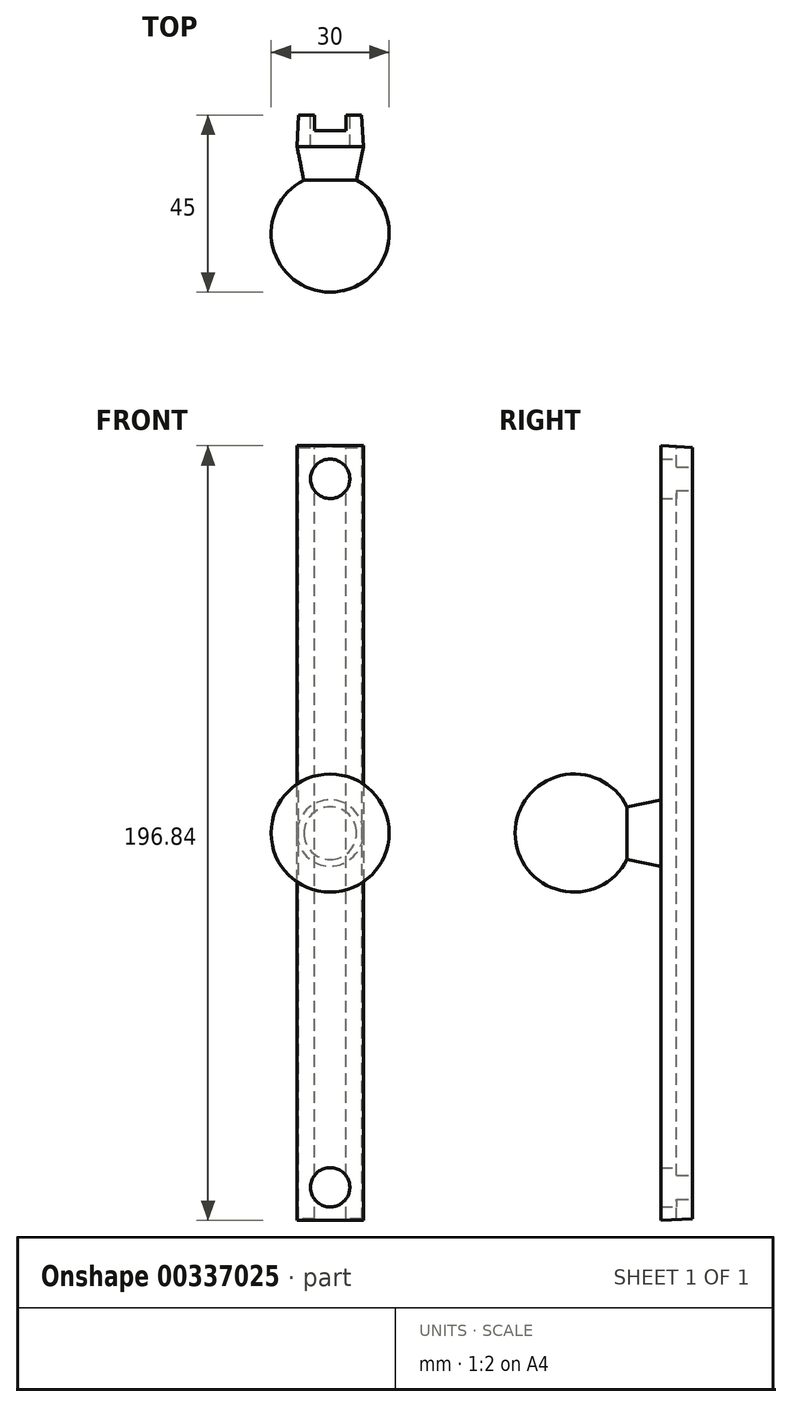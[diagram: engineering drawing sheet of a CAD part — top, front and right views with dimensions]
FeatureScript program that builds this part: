
annotation { "Feature Type Name" : "Feature", "Feature Type Description" : "" }
export const myFeature = defineFeature(function(context is Context, id is Id, definition is map)
    precondition{}
    {
        {
            var Q0;
            Q0=qCreatedBy(makeId("Front.planeOp"),FACE);
            var sketch = newSketch(context, id + "F0", { "sketchPlane" : qUnion([Q0])});
            skLineSegment(sketch, "E0.bottom", {"start": v(8, -98) * mm, "end": v(-8, -98) * mm});
            skLineSegment(sketch, "E0.top", {"start": v(8, 98) * mm, "end": v(-8, 98) * mm});
            skLineSegment(sketch, "E0.left", {"start": v(8, -98) * mm, "end": v(8, 98) * mm});
            skLineSegment(sketch, "E0.right", {"start": v(-8, -98) * mm, "end": v(-8, 98) * mm});
            skPoint(sketch, "E0.middle", {"position": v(0, 0) * mm});
            skSolve(sketch);
        }
        {
            var Q0;
            Q0 = qSketchRegion(id + "F0", true);
            extrude(context, id + "F1", {"entities" : qUnion([Q0]), "depth" : 8 * mm, "hasDraft" : true, "draftAngle" : 3 * degree});
        }
        {
            var Q0;
            Q0 = qSketchRegion(id + "F0", true);
            var sketch = newSketch(context, id + "F2", { "sketchPlane" : qUnion([Q0])});
            skLineSegment(sketch, "E1.bottom", {"start": v(4, -100) * mm, "end": v(-4, -100) * mm});
            skLineSegment(sketch, "E1.top", {"start": v(4, 100) * mm, "end": v(-4, 100) * mm});
            skLineSegment(sketch, "E1.left", {"start": v(4, -100) * mm, "end": v(4, 100) * mm});
            skLineSegment(sketch, "E1.right", {"start": v(-4, -100) * mm, "end": v(-4, 100) * mm});
            skPoint(sketch, "E1.middle", {"position": v(0, 0) * mm});
            skSolve(sketch);
        }
        {
            var Q0;
            Q0 = qSketchRegion(id + "F2", true);
            extrude(context, id + "F3", {"entities" : qUnion([Q0]), "operationType" : NewBodyOperationType.REMOVE, "depth" : 4 * mm});
        }
        {
            var Q0;
            Q0=qCreatedBy(makeId("Front.planeOp"),FACE);
            var sketch = newSketch(context, id + "F4", { "sketchPlane" : qUnion([Q0])});
            skCircle(sketch, "E2", {"center": v(0, 90) * mm, "radius": 5 * mm});
            skCircle(sketch, "E3", {"center": v(0, -90) * mm, "radius": 5 * mm});
            skSolve(sketch);
        }
        {
            var Q0;
            Q0 = qSketchRegion(id + "F4", true);
            extrude(context, id + "F5", {"entities" : qUnion([Q0]), "operationType" : NewBodyOperationType.REMOVE, "depth" : 25.4 * mm});
        }
        {
            var Q0;
            Q0=makeQuery(id+"F1.opExtrude","CAP_FACE",FACE,{"disambiguationData":[OSD([sQuery(id+"F0.wireOp",EDGE,"E0.bottom"),sQuery(id+"F0.wireOp",EDGE,"E0.top"),sQuery(id+"F0.wireOp",EDGE,"E0.left"),sQuery(id+"F0.wireOp",EDGE,"E0.right")])],"isStart":false});
            var sketch = newSketch(context, id + "F6", { "sketchPlane" : qUnion([Q0])});
            skCircle(sketch, "E4", {"center": v(0, 0) * mm, "radius": 8.42 * mm});
            skSolve(sketch);
        }
        {
            var Q0;
            Q0=qCreatedBy(makeId("Front.planeOp"),FACE);
            cPlane(context, id + "F7", {"entities" : qUnion([Q0]), "cplaneType" : CPlaneType.OFFSET, "offset" : 30 * mm, "width" : 152.4 * mm, "height" : 152.4 * mm});
        }
        {
            var Q0;
            Q0=qCreatedBy(id+"F7.planeOp",FACE);
            var sketch = newSketch(context, id + "F8", { "sketchPlane" : qUnion([Q0])});
            skCircle(sketch, "E5", {"center": v(0, 0) * mm, "radius": 4 * mm});
            skSolve(sketch);
        }
        {
            var Q1;
            Q1 = qSketchRegion(id + "F6", true);
            var Q2;
            Q2 = qSketchRegion(id + "F8", true);
            loft(context, id + "F9", {"operationType" : NewBodyOperationType.ADD, "sheetProfilesArray" : [{ "sheetProfileEntities" : qUnion([Q1]) }, { "sheetProfileEntities" : qUnion([Q2]) }]});
        }
        {
            var Q0;
            Q0=qCreatedBy(makeId("Top.planeOp"),FACE);
            var sketch = newSketch(context, id + "F10", { "sketchPlane" : qUnion([Q0])});
            skCircle(sketch, "E6", {"center": v(0, -30) * mm, "radius": 15 * mm, "construction": true});
            skLineSegment(sketch, "E7", {"start": v(0, -15) * mm, "end": v(0, -45) * mm, "construction": true});
            skArc(sketch, "E8", {"start": v(0, -15) * mm, "mid": v(-15, -30) * mm, "end": v(0, -45) * mm});
            skLineSegment(sketch, "E9", {"start": v(0, -15) * mm, "end": v(0, -45) * mm});
            skSolve(sketch);
        }
        {
            var Q0;
            Q0=makeQuery(id+"F10.imprint","IMPRINT",FACE,{"disambiguationData":[TD([[makeQuery(id+"F10.imprint","IMPRINT",EDGE,{"derivedFrom":sQuery(id+"F10.wireOp",EDGE,"E8")}),1.0]])]});
            var Q1;
            Q1=sQuery(id+"F10.wireOp",EDGE,"E9");
            revolve(context, id + "F11", {"operationType" : NewBodyOperationType.ADD, "entities" : qUnion([Q0]), "axis" : qUnion([Q1]), "revolveType" : RevolveType.FULL});
        }
        {
            var Q0;
            Q0=qCreatedBy(makeId("Right.planeOp"),FACE);
            cPlane(context, id + "F12", {"entities" : qUnion([Q0]), "cplaneType" : CPlaneType.OFFSET, "offset" : 25 * mm, "width" : 150 * mm, "height" : 150 * mm});
        }
        {
            var Q0;
            Q0=qCreatedBy(makeId("Right.planeOp"),FACE);
            cPlane(context, id + "F13", {"entities" : qUnion([Q0]), "cplaneType" : CPlaneType.OFFSET, "offset" : 25 * mm, "oppositeDirection" : true, "width" : 150 * mm, "height" : 150 * mm});
        }
        {
            var Q0;
            Q0=qCreatedBy(id+"F13.planeOp",FACE);
            var sketch = newSketch(context, id + "F14", { "sketchPlane" : qUnion([Q0])});
            skCircle(sketch, "E10", {"center": v(-29.95, 0) * mm, "radius": 17.91 * mm});
            skSolve(sketch);
        }
        {
            var Q0;
            Q0=qCreatedBy(id+"F12.planeOp",FACE);
            var sketch = newSketch(context, id + "F15", { "sketchPlane" : qUnion([Q0])});
            skCircle(sketch, "E11", {"center": v(-30, 0) * mm, "radius": 17.8 * mm});
            skSolve(sketch);
        }
        {
            var Q0;
            Q0=makeQuery(id+"F15.imprint","IMPRINT",FACE,{"disambiguationData":[TD([[makeQuery(id+"F15.imprint","IMPRINT",EDGE,{"derivedFrom":sQuery(id+"F15.wireOp",EDGE,"E11")}),1.0]])]});
            extrude(context, id + "F16", {"entities" : qUnion([Q0]), "operationType" : NewBodyOperationType.REMOVE, "depth" : 25 * mm});
        }
        {
            var Q0;
            Q0=makeQuery(id+"F14.imprint","IMPRINT",FACE,{"disambiguationData":[TD([[makeQuery(id+"F14.imprint","IMPRINT",EDGE,{"derivedFrom":sQuery(id+"F14.wireOp",EDGE,"E10")}),1.0]])]});
            extrude(context, id + "F17", {"entities" : qUnion([Q0]), "operationType" : NewBodyOperationType.REMOVE, "oppositeDirection" : true, "depth" : 25 * mm});
        }
    });
